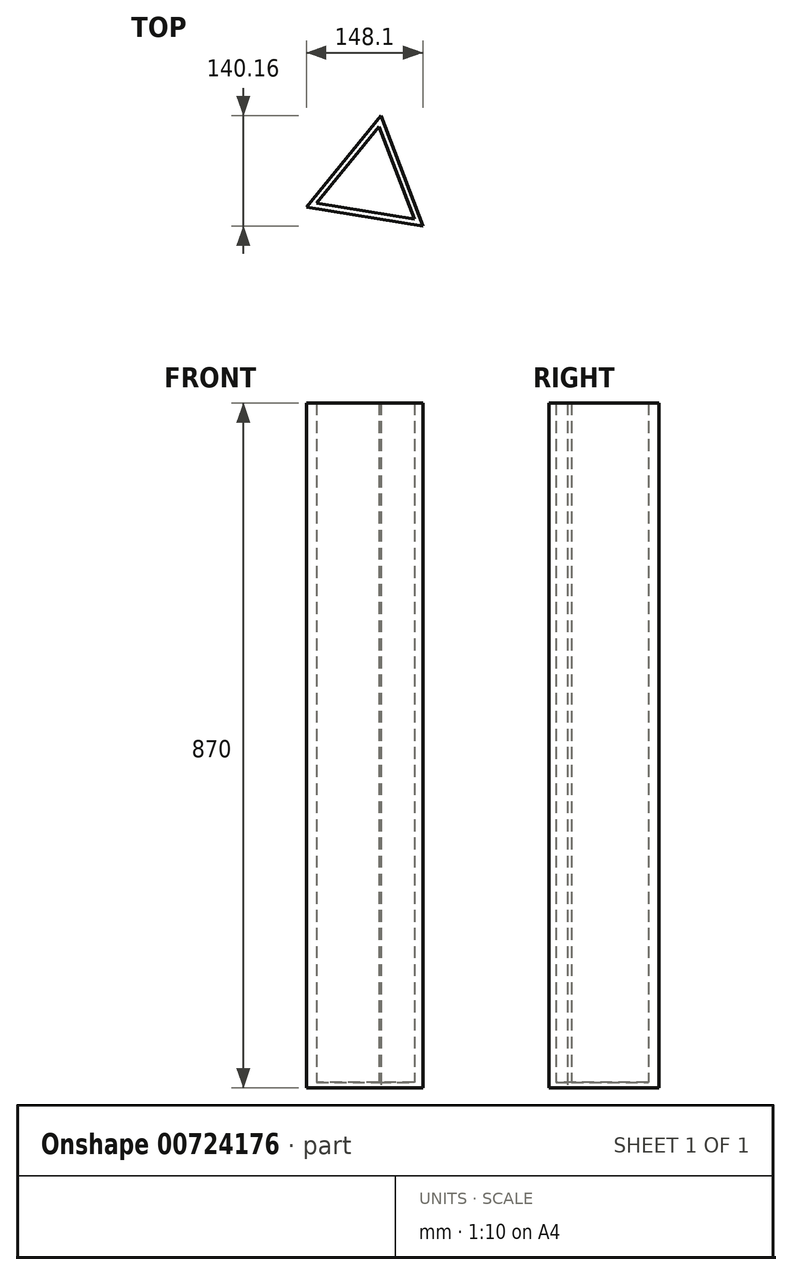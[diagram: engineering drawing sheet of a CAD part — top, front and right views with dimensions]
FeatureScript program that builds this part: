
annotation { "Feature Type Name" : "Feature", "Feature Type Description" : "" }
export const myFeature = defineFeature(function(context is Context, id is Id, definition is map)
    precondition{}
    {
        {
            var Q0;
            Q0=qCreatedBy(makeId("Top.planeOp"),FACE);
            var sketch = newSketch(context, id + "F0", { "sketchPlane" : qUnion([Q0])});
            skCircle(sketch, "E0.cCircle", {"center": v(0, 0) * mm, "radius": 43.3 * mm, "construction": true});
            skLineSegment(sketch, "E0.0", {"start": v(-80.92, -30.85) * mm, "end": v(13.74, 85.5) * mm});
            skLineSegment(sketch, "E0.1", {"start": v(13.74, 85.5) * mm, "end": v(67.18, -54.65) * mm});
            skLineSegment(sketch, "E0.2", {"start": v(67.18, -54.65) * mm, "end": v(-80.92, -30.85) * mm});
            skPoint(sketch, "E0.0.midPoint", {"position": v(-33.6, 27.33) * mm});
            skSolve(sketch);
        }
        {
            var Q0;
            Q0=makeQuery(id+"F0.imprint","IMPRINT",FACE,{"disambiguationData":[TD([[makeQuery(id+"F0.imprint","IMPRINT",EDGE,{"derivedFrom":sQuery(id+"F0.wireOp",EDGE,"E0.0")}),-1.0]])]});
            extrude(context, id + "F1", {"entities" : qUnion([Q0]), "depth" : 870 * mm, "offsetDistance" : 25 * mm});
        }
        {
            var Q0;
            Q0=makeQuery(id+"F1.opExtrude","CAP_FACE",FACE,{"disambiguationData":[OSD([sQuery(id+"F0.wireOp",EDGE,"E0.0"),sQuery(id+"F0.wireOp",EDGE,"E0.1"),sQuery(id+"F0.wireOp",EDGE,"E0.2")])],"isStart":false});
            shell(context, id + "F2", {"entities" : qUnion([Q0]), "thickness" : 7 * mm});
        }
    });
